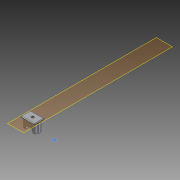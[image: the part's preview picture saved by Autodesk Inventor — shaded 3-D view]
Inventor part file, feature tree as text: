
AUTODESK INVENTOR PART (.ipt)
format: ipt  version: 2012 (Build 160160000, 160)  size: 251,904 bytes
history: native  units: in
note: dims shown in document units (in); Inventor stores cm internally (conversion verified against a paired STEP export)
features: sketch x8, extrude x8, reference x5, projected_geometry x5, fillet x3, plane x2
ambient origin geometry x8: Origin, YZ Plane, XZ Plane, XY Plane, X Axis, Y Axis, Z Axis, Center Point
feature tree (31):
  plane  "Work Plane8"
  sketch  "Sketch21"  dims[d99=0.0118in d100=0.0118in]
  plane  "Work Plane9"
  extrude  "Extrusion20"  Depth=0.0118in
  extrude  "Extrusion21"  Depth=0.0118in
  extrude  "Extrusion22"  Depth=0.0118in
  extrude  "Extrusion23"  Depth=0.0118in
  sketch  "Sketch25"  dims[d108=0.0118in d109=0.0118in d110=0.0118in d111=0.3937in d112=0.0in]
  fillet  "Fillet13"  Radius=0.0118in
  extrude  "Extrusion24"  Depth=0.0118in
  fillet  "Fillet14"  Radius=0.0118in
  fillet  "Fillet15"  Radius=0.3937in
  extrude  "Extrusion25"  Depth=0.0984in
  extrude  "Extrusion26"  Depth=0.0118in
  extrude  "Extrusion27"  Depth=0.0591in TaperAngle=0.0deg
  reference  "Reference41"
  sketch  "Sketch22"  dims[d101=0.0118in d102=0.0118in]
  reference  "Reference42"
  sketch  "Sketch23"  dims[d103=0.0118in d104=0.0118in]
  projected_geometry  "Projected Loop8"
  reference  "Reference43"
  reference  "Reference44"
  sketch  "Sketch24"  dims[d105=0.0118in d106=0.0118in d107=0.0118in]
  projected_geometry  "Projected Loop9"
  reference  "Reference45"
  sketch  "Sketch26"  dims[d113=0.3937in d114=0.0in d115=0.0984in]
  projected_geometry  "Projected Loop10"
  projected_geometry  "Projected Loop11"
  sketch  "Sketch27"  dims[d116=0.0984in d117=0.0118in]
  projected_geometry  "Projected Loop12"
  sketch  "Sketch28"  dims[d118=0.0118in d119=0.0591in d120=0.0in d121=0.8016in d122=0.2672in d123=0.2672in d124=0.0295in d125=0.0591in d126=0.0591in d127=0.0in d128=0.0787in d129=0.0591in d130=0.0in d131=0.0787in d132=0.0394in d133=0.0059in d134=0.0in d135=0.0059in d136=0.0in d137=0.1969in d138=0.0in]
